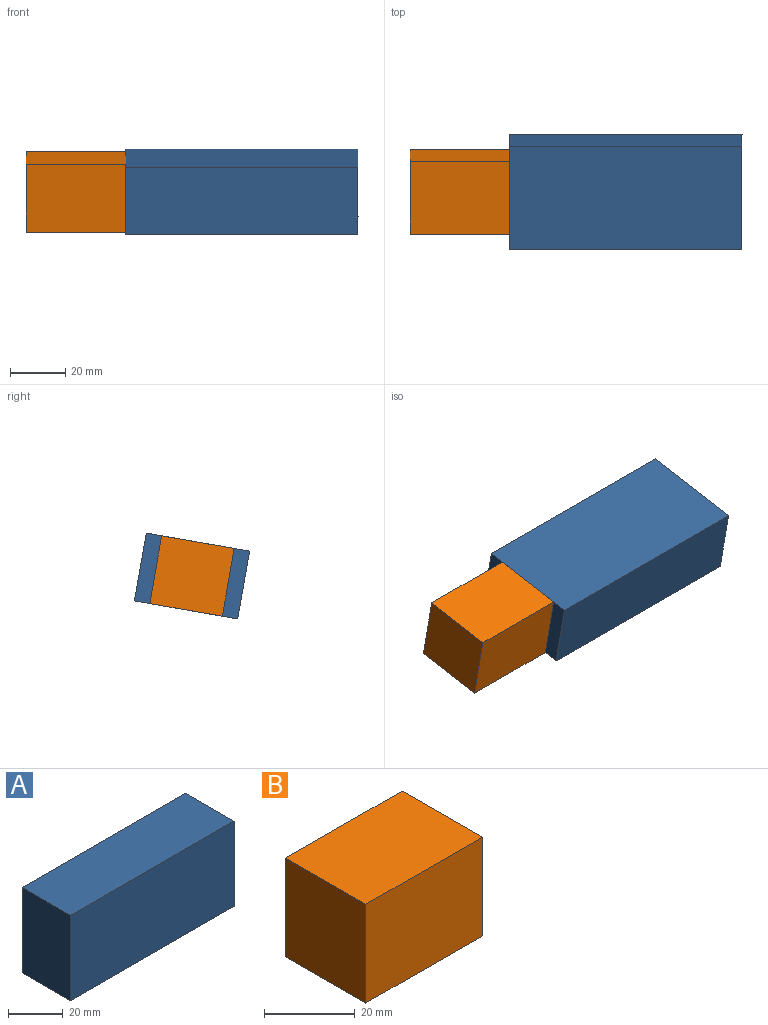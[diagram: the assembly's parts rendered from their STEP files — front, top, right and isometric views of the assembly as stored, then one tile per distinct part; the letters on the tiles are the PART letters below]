
ASSEMBLY  parts=2 mates=1
PART A: 6 faces, bbox 84.3x25x38.1 mm
  f0: plane 84.32x25mm, normal (0,0,1), area 2108.1mm2, adj f1,f3,f4,f5
  f1: plane 38.09x25mm, normal (-1,0,0), area 952.1mm2, adj f0,f2,f4,f5
  f2: plane 84.32x25mm, normal (0,0,-1), area 2108.1mm2, adj f1,f3,f4,f5
  f3: plane 38.09x25mm, normal (1,0,0), area 952.1mm2, adj f0,f2,f4,f5
  f4: plane 84.32x38.09mm, normal (0,-1,0), area 3211.5mm2, adj f0,f1,f2,f3
  f5: plane 84.32x38.09mm, normal (0,1,0), area 3211.5mm2, adj f0,f1,f2,f3
PART B: 6 faces, bbox 36.3x25x26.7 mm
  f0: plane 36.26x25mm, normal (0,0,1), area 906.5mm2, adj f1,f3,f4,f5
  f1: plane 26.7x25mm, normal (-1,0,0), area 667.6mm2, adj f0,f2,f4,f5
  f2: plane 36.26x25mm, normal (0,0,-1), area 906.5mm2, adj f1,f3,f4,f5
  f3: plane 26.7x25mm, normal (1,0,0), area 667.6mm2, adj f0,f2,f4,f5
  f4: plane 36.26x26.7mm, normal (0,-1,0), area 968.2mm2, adj f0,f1,f2,f3
  f5: plane 36.26x26.7mm, normal (0,1,0), area 968.2mm2, adj f0,f1,f2,f3
PLACE A rot(axis=(1,0,0),99.9deg) t=(-9.19,-23.82,45.27)mm
PLACE B rot(axis=(1,0,0),99.9deg) t=(18.08,5.32,50.35)mm
MATE revolute B.f3 <-> A.f1  axis (1,0,0) through (-108.83,-40.43,29.68)mm
